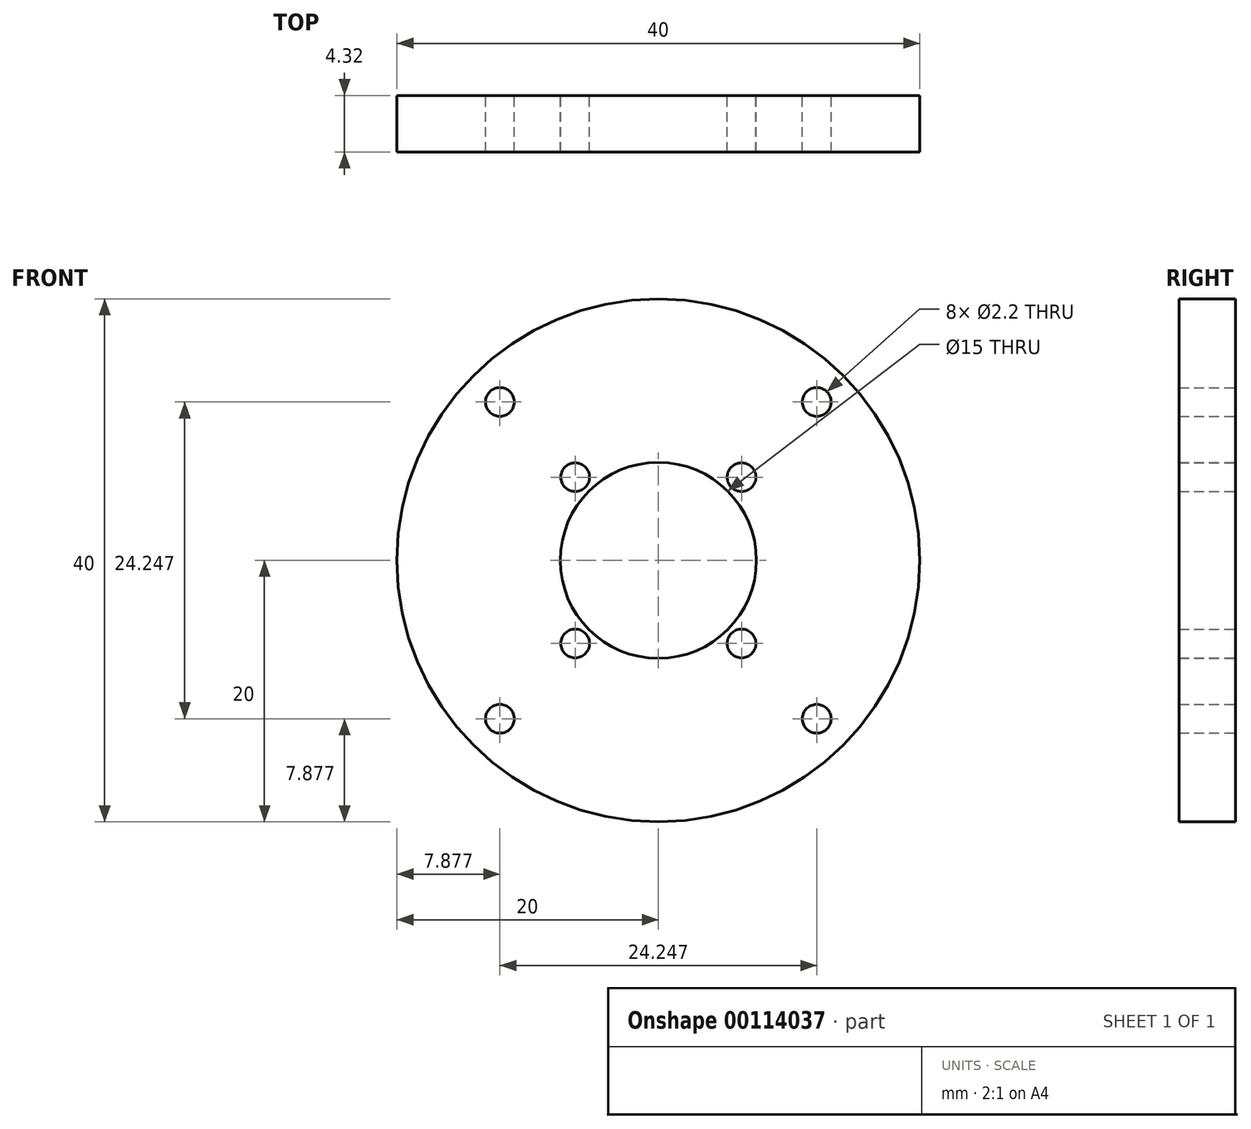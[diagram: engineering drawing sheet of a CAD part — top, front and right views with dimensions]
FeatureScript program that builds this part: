
annotation { "Feature Type Name" : "Feature", "Feature Type Description" : "" }
export const myFeature = defineFeature(function(context is Context, id is Id, definition is map)
    precondition{}
    {
        {
            var Q0;
            Q0=qCreatedBy(makeId("Front.planeOp"),FACE);
            var sketch = newSketch(context, id + "F0", { "sketchPlane" : qUnion([Q0])});
            skCircle(sketch, "E0", {"center": v(0, 0) * mm, "radius": 20 * mm});
            skCircle(sketch, "E1", {"center": v(0, 0) * mm, "radius": 7.5 * mm});
            skCircle(sketch, "E2", {"center": v(0, 0) * mm, "radius": 9 * mm, "construction": true});
            skLineSegment(sketch, "E3", {"start": v(0, 0) * mm, "end": v(6.36, 6.36) * mm, "construction": true});
            skCircle(sketch, "E4", {"center": v(6.36, 6.36) * mm, "radius": 1.1 * mm});
            skCircle(sketch, "E5.1.0", {"center": v(-6.36, 6.36) * mm, "radius": 1.1 * mm});
            skCircle(sketch, "E5.2.0", {"center": v(-6.36, -6.36) * mm, "radius": 1.1 * mm});
            skCircle(sketch, "E5.3.0", {"center": v(6.36, -6.36) * mm, "radius": 1.1 * mm});
            skCircle(sketch, "E6", {"center": v(0, 0) * mm, "radius": 17.15 * mm, "construction": true});
            skLineSegment(sketch, "E7", {"start": v(0, 0) * mm, "end": v(12.12, 12.12) * mm, "construction": true});
            skCircle(sketch, "E8", {"center": v(12.12, 12.12) * mm, "radius": 1.1 * mm});
            skCircle(sketch, "E9.1.0", {"center": v(-12.12, 12.12) * mm, "radius": 1.1 * mm});
            skCircle(sketch, "E9.2.0", {"center": v(-12.12, -12.12) * mm, "radius": 1.1 * mm});
            skCircle(sketch, "E9.3.0", {"center": v(12.12, -12.12) * mm, "radius": 1.1 * mm});
            skSolve(sketch);
        }
        {
            var Q0;
            Q0 = qSketchRegion(id + "F0", true);
            extrude(context, id + "F1", {"entities" : qUnion([Q0]), "depth" : 4.32 * mm});
        }
    });
